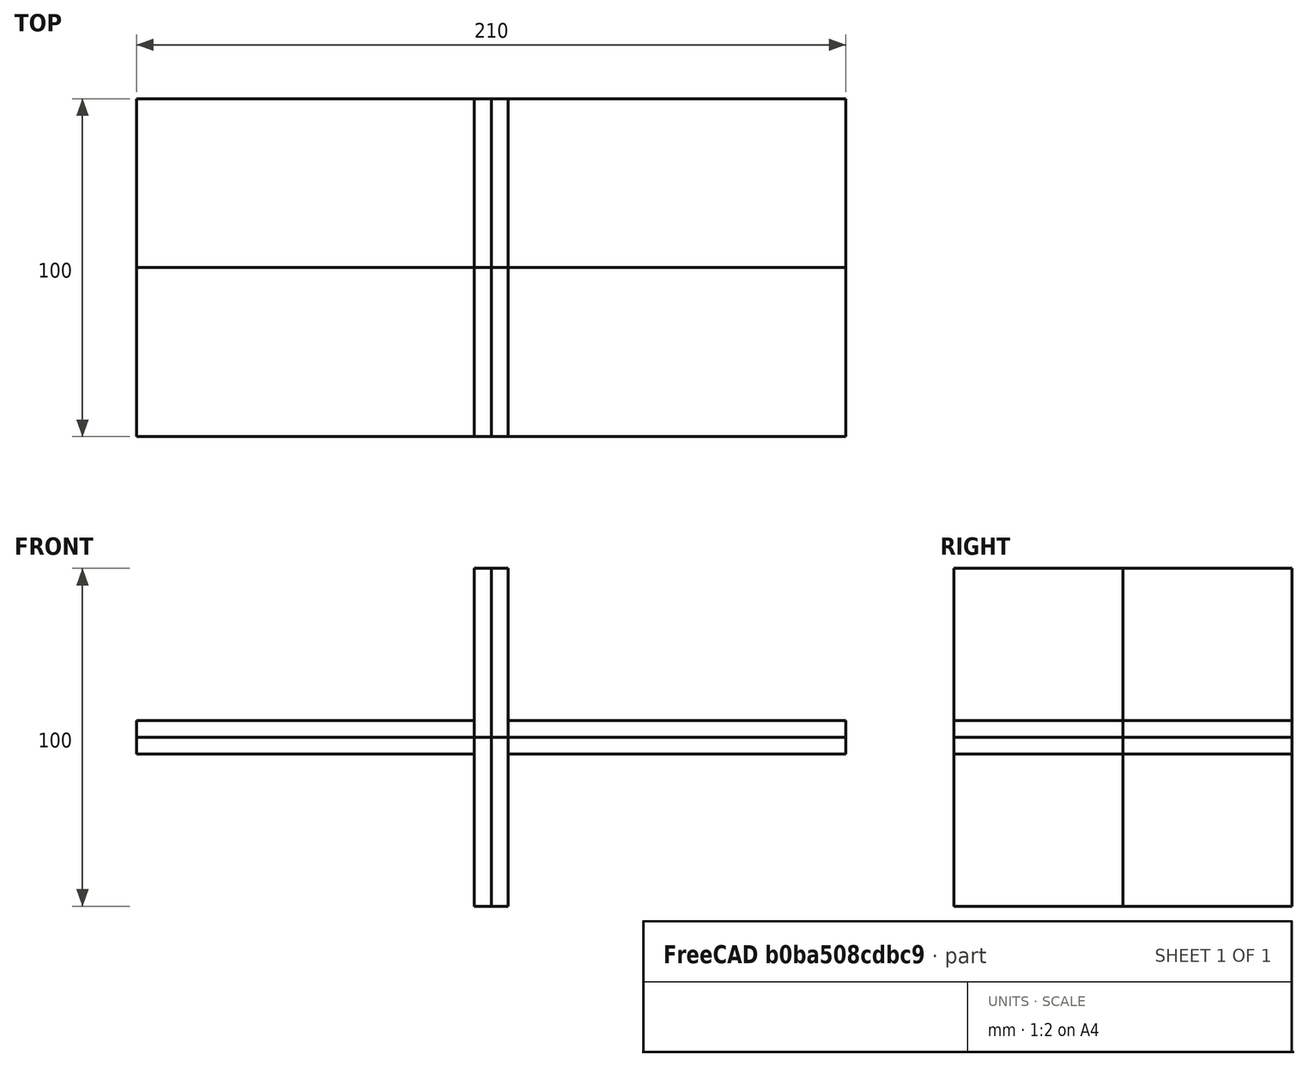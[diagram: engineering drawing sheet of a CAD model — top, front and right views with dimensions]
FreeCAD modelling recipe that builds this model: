
FCSTD DOCUMENT  (FreeCAD 0.21R33694 (Git))
Label: Cruciform Fillet Test (no welds)
License: All rights reserved
LicenseURL: http://en.wikipedia.org/wiki/All_rights_reserved
objects: Part::Box×16, Part::FeaturePython×13, Fem::ConstraintDisplacement×3, Part::Mirroring×2, Fem::ConstraintPressure×2, App::MaterialObjectPython×1, Fem::FemSolverObjectPython×1, Fem::FeaturePython×1, Fem::FemMeshObjectPython×1, Fem::FemAnalysis×1
note: 31 computed .brp shape members not serialized (recipe doc carries the construction recipe); baked Part::Feature solids carry a one-line shape summary decoded from their .brp

FEATURE [Part::Box] Box  label="plate"
  AttacherType = Attacher::AttachEngine3D
  Height = 5
  Length = 100
  Width = 50
FEATURE [App::MaterialObjectPython] MaterialSolid  # material (typed FeaturePython)
  Category = 0
  Material = AuthorAndLicense=(c) 2014 M. Münch - GNU Lesser General Public License (LGPL),CardName=Steel-St-E-315,Density=7800 kg/m^3,Father=Metal,+13 more (map truncated)
FEATURE [Fem::FemSolverObjectPython] SolverCcxTools  # FEM object (typed FeaturePython)
  AnalysisType = 0
  BeamShellResultOutput3D = false
  BucklingFactors = 1
  EigenmodeHighLimit = 1000000
  EigenmodeLowLimit = 0
  EigenmodesCount = 10
  GeometricalNonlinearity = 0
  IterationsControlParameterCutb = 0.25,0.5,0.75,0.85,,,1.5,
  IterationsControlParameterIter = 4,8,9,200,10,400,,200,,
  IterationsControlParameterTimeUse = false
  IterationsThermoMechMaximum = 2000
  IterationsUserDefinedIncrementations = false
  IterationsUserDefinedTimeStepLength = false
  MaterialNonlinearity = 0
  MatrixSolverType = 0
  SplitInputWriter = false
  ThermoMechSteadyState = true
  TimeEnd = 1
  TimeInitialStep = 0.01
FEATURE [Part::Box] Box002  label="plate002"
  AttacherType = Attacher::AttachEngine3D
  Height = 5
  Length = 50
  Placement = pos=(-5,0,5) rot=(0,1,0;1.5708rad)
  Width = 50
FEATURE [Fem::ConstraintDisplacement] ConstraintDisplacement
  NormalDirection = (-1,0,0)
  Normals = (16) [(-1,0,0),(-1,0,0),(-1,0,0),(-1,0,0),(-1,0,0),(-1,0,0),(-1,0,0),(-1,0,0),(-1,0,0),(-1,0,0),(-1,0,0),(-1,0,0),(-1,0,0),(-1,0,0),(-1,0,0),(-1,0,0)]
  Points = (16) [(-5,0,5),(-5,0,-11.6667),(-5,0,-28.3333),(-5,0,-45),(-5,16.6667,5),(-5,16.6667,-11.6667),(-5,16.6667,-28.3333),(-5,16.6667,-45),(-5,33.3333,5),+7 more]
  References = -> [Box002]
  Scale = 6
  hasXFormula = false
  hasYFormula = false
  hasZFormula = false
  rotxFix = false
  rotxFree = true
  rotyFix = false
  rotyFree = true
  rotzFix = false
  rotzFree = true
  useFlowSurfaceForce = false
  xDisplacement = 0
  xFix = false
  xFree = false
  xRotation = 0
  yDisplacement = 0
  yFix = false
  yFree = true
  yRotation = 0
  zDisplacement = 0
  zFix = false
  zFree = true
  zRotation = 0
FEATURE [Fem::ConstraintDisplacement] ConstraintDisplacement002
  NormalDirection = (0,0,1)
  Normals = (28) [(0,0,1),(0,0,1),(0,0,1),(0,0,1),(0,0,1),(0,0,1),(0,0,1),(0,0,1),(0,0,1),(0,0,1),(0,0,1),(0,0,1),(0,0,1),(0,0,1),(0,0,1),(0,0,1),(0,0,1),(0,0,1),+10 more]
  Points = (28) [(0,0,5),(33.3333,0,5),(66.6667,0,5),(100,0,5),(0,16.6667,5),(33.3333,16.6667,5),(66.6667,16.6667,5),(100,16.6667,5),(0,33.3333,5),(33.3333,33.3333,5),+18 more]
  References = -> [Box,Box002]
  hasXFormula = false
  hasYFormula = false
  hasZFormula = false
  rotxFix = false
  rotxFree = true
  rotyFix = false
  rotyFree = true
  rotzFix = false
  rotzFree = true
  useFlowSurfaceForce = false
  xDisplacement = 0
  xFix = false
  xFree = true
  xRotation = 0
  yDisplacement = 0
  yFix = false
  yFree = true
  yRotation = 0
  zDisplacement = 0
  zFix = true
  zFree = false
  zRotation = 0
FEATURE [Part::FeaturePython] BooleanFragments  # WARN: FeaturePython — macro-defined, semantics opaque (R4)
  Mode = 2
  Objects = -> [Box,Box002]
  Tolerance = 0
FEATURE [Fem::ConstraintDisplacement] ConstraintDisplacement003
  NormalDirection = (0,1,0)
  Normals = (24) [(0,1,0),(0,1,0),(0,1,0),(0,1,0),(0,1,0),(0,1,0),(0,1,0),(0,1,0),(0,1,0),(0,1,0),(0,1,0),(0,1,0),(0,1,0),(0,1,0),(0,1,0),(0,1,0),(0,1,0),(0,1,0),+6 more]
  Points = (24) [(-5,50,5),(-2.5,50,5),(0,50,5),(-5,50,-11.6667),(-2.5,50,-11.6667),(0,50,-11.6667),(-5,50,-28.3333),(-2.5,50,-28.3333),(0,50,-28.3333),(-5,50,-45),+14 more]
  References = -> [BooleanFragments]
  hasXFormula = false
  hasYFormula = false
  hasZFormula = false
  rotxFix = false
  rotxFree = true
  rotyFix = false
  rotyFree = true
  rotzFix = false
  rotzFree = true
  useFlowSurfaceForce = false
  xDisplacement = 0
  xFix = false
  xFree = true
  xRotation = 0
  yDisplacement = 0
  yFix = true
  yFree = false
  yRotation = 0
  zDisplacement = 0
  zFix = false
  zFree = true
  zRotation = 0
FEATURE [Part::Box] Box003  label="plate003"
  AttacherType = Attacher::AttachEngine3D
  Height = 5
  Length = 100
  Width = 50
FEATURE [Part::Box] Box004  label="plate004"
  AttacherType = Attacher::AttachEngine3D
  Height = 5
  Length = 50
  Placement = pos=(-5,0,5) rot=(0,1,0;1.5708rad)
  Width = 50
FEATURE [Part::FeaturePython] BooleanFragments001  # WARN: FeaturePython — macro-defined, semantics opaque (R4)
  Mode = 2
  Objects = -> [Box003,Box004]
  Placement = pos=(0,50,0) rot=(0,0,1;0rad)
  Tolerance = 0
FEATURE [Part::FeaturePython] BooleanFragments002  # WARN: FeaturePython — macro-defined, semantics opaque (R4)
  Mode = 0
  Objects = -> [BooleanFragments,BooleanFragments001]
  Tolerance = 0
FEATURE [Part::Box] Box005  label="plate005"
  AttacherType = Attacher::AttachEngine3D
  Height = 5
  Length = 100
  Width = 50
FEATURE [Part::Box] Box006  label="plate006"
  AttacherType = Attacher::AttachEngine3D
  Height = 5
  Length = 50
  Placement = pos=(-5,0,5) rot=(0,1,0;1.5708rad)
  Width = 50
FEATURE [Part::FeaturePython] BooleanFragments003  # WARN: FeaturePython — macro-defined, semantics opaque (R4)
  Mode = 2
  Objects = -> [Box005,Box006]
  Tolerance = 0
FEATURE [Part::Box] Box007  label="plate007"
  AttacherType = Attacher::AttachEngine3D
  Height = 5
  Length = 100
  Width = 50
FEATURE [Part::Box] Box008  label="plate008"
  AttacherType = Attacher::AttachEngine3D
  Height = 5
  Length = 50
  Placement = pos=(-5,0,5) rot=(0,1,0;1.5708rad)
  Width = 50
FEATURE [Part::FeaturePython] BooleanFragments004  # WARN: FeaturePython — macro-defined, semantics opaque (R4)
  Mode = 2
  Objects = -> [Box007,Box008]
  Placement = pos=(0,50,0) rot=(0,0,1;0rad)
  Tolerance = 0
FEATURE [Part::FeaturePython] BooleanFragments005  # WARN: FeaturePython — macro-defined, semantics opaque (R4)
  Mode = 0
  Objects = -> [BooleanFragments003,BooleanFragments004]
  Placement = pos=(-10,0,10) rot=(0,1,0;3.14159rad)
  Tolerance = 0
FEATURE [Part::Box] Box009  label="plate009"
  AttacherType = Attacher::AttachEngine3D
  Height = 5
  Length = 100
  Width = 50
FEATURE [Part::Box] Box010  label="plate010"
  AttacherType = Attacher::AttachEngine3D
  Height = 5
  Length = 50
  Placement = pos=(-5,0,5) rot=(0,1,0;1.5708rad)
  Width = 50
FEATURE [Part::FeaturePython] BooleanFragments006  # WARN: FeaturePython — macro-defined, semantics opaque (R4)
  Mode = 2
  Objects = -> [Box009,Box010]
  Tolerance = 0
FEATURE [Part::Box] Box011  label="plate011"
  AttacherType = Attacher::AttachEngine3D
  Height = 5
  Length = 100
  Width = 50
FEATURE [Part::Box] Box012  label="plate012"
  AttacherType = Attacher::AttachEngine3D
  Height = 5
  Length = 50
  Placement = pos=(-5,0,5) rot=(0,1,0;1.5708rad)
  Width = 50
FEATURE [Part::FeaturePython] BooleanFragments007  # WARN: FeaturePython — macro-defined, semantics opaque (R4)
  Mode = 2
  Objects = -> [Box011,Box012]
  Placement = pos=(0,50,0) rot=(0,0,1;0rad)
  Tolerance = 0
FEATURE [Part::FeaturePython] BooleanFragments008  # WARN: FeaturePython — macro-defined, semantics opaque (R4)
  Mode = 0
  Objects = -> [BooleanFragments006,BooleanFragments007]
  Placement = pos=(-10,0,10) rot=(0,1,0;3.14159rad)
  Tolerance = 0
FEATURE [Part::Mirroring] Part__Mirroring  label="BooleanFragments008 (Mirror #1)"
  Base = (0,0,0)
  Normal = (1,0,0)
  Placement = pos=(-10,0,0) rot=(0,0,1;0rad)
  Source = -> BooleanFragments008
FEATURE [Part::Box] Box013  label="plate013"
  AttacherType = Attacher::AttachEngine3D
  Height = 5
  Length = 100
  Width = 50
FEATURE [Part::Box] Box014  label="plate014"
  AttacherType = Attacher::AttachEngine3D
  Height = 5
  Length = 50
  Placement = pos=(-5,0,5) rot=(0,1,0;1.5708rad)
  Width = 50
FEATURE [Part::FeaturePython] BooleanFragments009  # WARN: FeaturePython — macro-defined, semantics opaque (R4)
  Mode = 2
  Objects = -> [Box013,Box014]
  Tolerance = 0
FEATURE [Part::Box] Box015  label="plate015"
  AttacherType = Attacher::AttachEngine3D
  Height = 5
  Length = 100
  Width = 50
FEATURE [Part::Box] Box016  label="plate016"
  AttacherType = Attacher::AttachEngine3D
  Height = 5
  Length = 50
  Placement = pos=(-5,0,5) rot=(0,1,0;1.5708rad)
  Width = 50
FEATURE [Part::FeaturePython] BooleanFragments010  # WARN: FeaturePython — macro-defined, semantics opaque (R4)
  Mode = 2
  Objects = -> [Box015,Box016]
  Placement = pos=(0,50,0) rot=(0,0,1;0rad)
  Tolerance = 0
FEATURE [Part::FeaturePython] BooleanFragments011  # WARN: FeaturePython — macro-defined, semantics opaque (R4)
  Mode = 0
  Objects = -> [BooleanFragments009,BooleanFragments010]
  Tolerance = 0
FEATURE [Part::Mirroring] Part__Mirroring001  label="BooleanFragments011 (Mirror #2)"
  Base = (0,0,0)
  Normal = (1,0,0)
  Placement = pos=(-10,0,0) rot=(0,0,1;0rad)
  Source = -> BooleanFragments011
FEATURE [Part::FeaturePython] BooleanFragments012  # WARN: FeaturePython — macro-defined, semantics opaque (R4)
  Mode = 0
  Objects = -> [BooleanFragments002,BooleanFragments005,Part__Mirroring,Part__Mirroring001]
  Tolerance = 0
FEATURE [Fem::FeaturePython] MeshRegion  # FEM object (typed FeaturePython)
  CharacteristicLength = 1
  References = -> [Box]
FEATURE [Fem::FemMeshObjectPython] FEMMeshGmsh  # FEM object (typed FeaturePython)
  Algorithm2D = 0
  Algorithm3D = 0
  CharacteristicLengthMax = 5
  CharacteristicLengthMin = 0
  CoherenceMesh = true
  ElementDimension = 0
  ElementOrder = 1
  GeometryTolerance = 1e-06
  GroupsOfNodes = false
  HighOrderOptimize = 0
  MeshRegionList = -> [MeshRegion]
  MeshSizeFromCurvature = 12
  OptimizeNetgen = false
  OptimizeStd = true
  Part = -> BooleanFragments
  RecombinationAlgorithm = 0
  Recombine3DAll = false
  RecombineAll = false
  SecondOrderLinear = false
FEATURE [Fem::ConstraintPressure] ConstraintPressure
  NormalDirection = (1,0,0)
  Normals = (96) [(1,0,0),(1,0,0),(1,0,0),(1,0,0),(1,0,0),(1,0,0),(1,0,0),(1,0,0),(1,0,0),(1,0,0),(1,0,0),(1,0,0),(1,0,0),(1,0,0),(1,0,0),(1,0,0),(1,0,0),(1,0,0),+78 more]
  Points = (96) [(100,100,0),(100,100,2.5),(100,100,5),(100,83.3333,0),(100,83.3333,2.5),(100,83.3333,5),(100,66.6667,0),(100,66.6667,2.5),(100,66.6667,5),(100,50,0),+86 more]
  Pressure = 100
  References = -> [BooleanFragments012]
  Reversed = true
FEATURE [Fem::ConstraintPressure] ConstraintPressure001
  NormalDirection = (0,0,-1)
  Normals = (96) [(0,0,-1),(0,0,-1),(0,0,-1),(0,0,-1),(0,0,-1),(0,0,-1),(0,0,-1),(0,0,-1),(0,0,-1),(0,0,-1),(0,0,-1),(0,0,-1),(0,0,-1),(0,0,-1),(0,0,-1),(0,0,-1),+80 more]
  Points = (96) [(-5,100,-45),(-2.5,100,-45),(0,100,-45),(-5,83.3333,-45),(-2.5,83.3333,-45),(0,83.3333,-45),(-5,66.6667,-45),(-2.5,66.6667,-45),(0,66.6667,-45),+87 more]
  Pressure = 1e-06
  References = -> [BooleanFragments012]
  Reversed = true
FEATURE [Fem::FemAnalysis] Analysis
  Group = -> [MaterialSolid,SolverCcxTools,ConstraintDisplacement,ConstraintDisplacement002,ConstraintDisplacement003,FEMMeshGmsh,ConstraintPressure,ConstraintPressure001]
